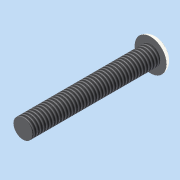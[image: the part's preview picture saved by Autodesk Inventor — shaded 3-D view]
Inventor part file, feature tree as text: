
AUTODESK INVENTOR PART (.ipt)
format: ipt  version: 2015 (Build 190159000, 159)  size: 97,280 bytes
history: native  units: mm
features: revolve x1, fillet x1, thread x1, sketch x1
ambient origin geometry x8: Origin, YZ Plane, XZ Plane, XY Plane, X Axis, Y Axis, Z Axis, Center Point
bodies: Solid1 (feature_tree)
feature tree (4):
  revolve  "Revolution1"  [1 undecoded]
  fillet  "Fillet1"  Radius=1.0mm
  thread  "Thread1"  [1 undecoded]
  sketch  "Sketch1"  dims[d0=1.5mm d1=2.5mm d2=1.0mm d3=90.0deg d4=1.0mm d5=10.0mm d6=0.0mm d7=20.0mm]
note: 2 required parameter values undecoded (feature->parameter linkage not recoverable at this tier; creation-order binding heuristic only, values carry confidence <= 0.55)